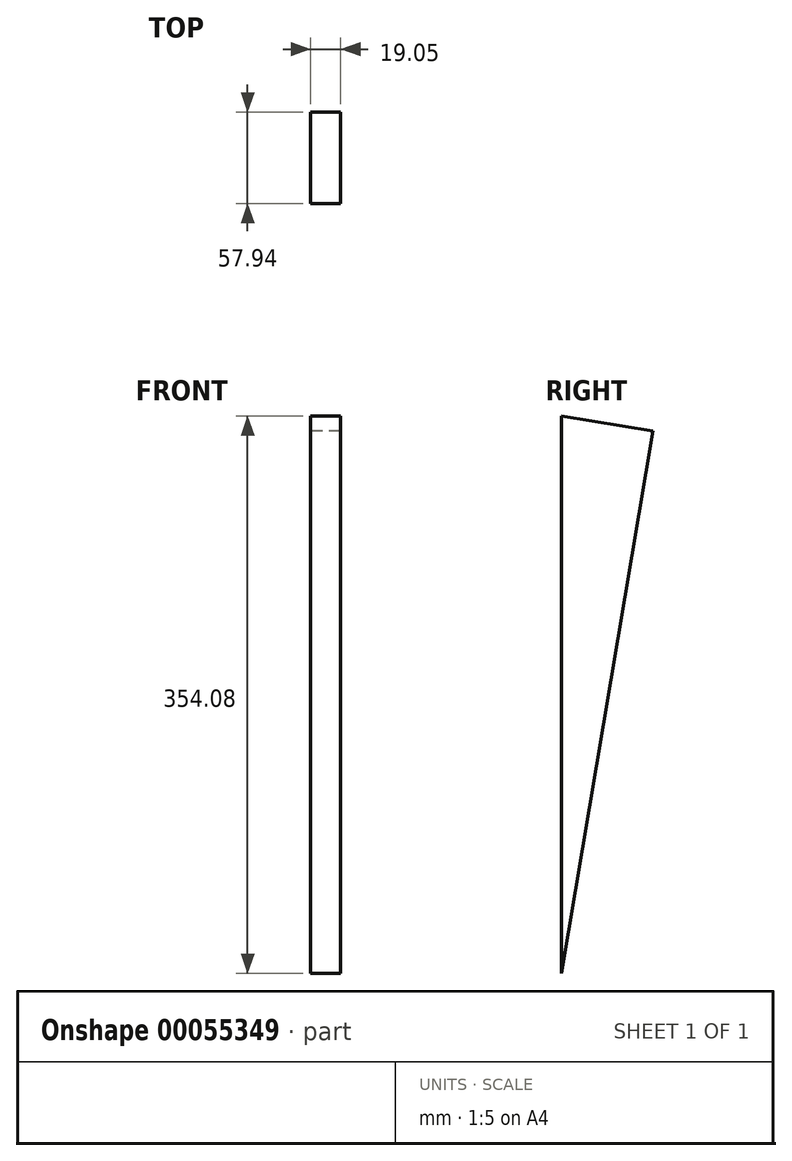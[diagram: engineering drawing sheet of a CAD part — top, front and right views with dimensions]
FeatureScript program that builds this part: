
annotation { "Feature Type Name" : "Feature", "Feature Type Description" : "" }
export const myFeature = defineFeature(function(context is Context, id is Id, definition is map)
    precondition{}
    {
        {
            var Q0;
            Q0=qCreatedBy(makeId("Right.planeOp"),FACE);
            var sketch = newSketch(context, id + "F0", { "sketchPlane" : qUnion([Q0])});
            skLineSegment(sketch, "E0", {"start": v(0, 0) * mm, "end": v(0, 354.08) * mm});
            skLineSegment(sketch, "E1", {"start": v(0, 0) * mm, "end": v(57.94, 344.41) * mm});
            skLineSegment(sketch, "E2", {"start": v(57.94, 344.41) * mm, "end": v(0, 354.08) * mm});
            skSolve(sketch);
        }
        {
            var Q0;
            Q0 = qSketchRegion(id + "F0", true);
            extrude(context, id + "F1", {"entities" : qUnion([Q0]), "depth" : 19.05 * mm});
        }
    });
